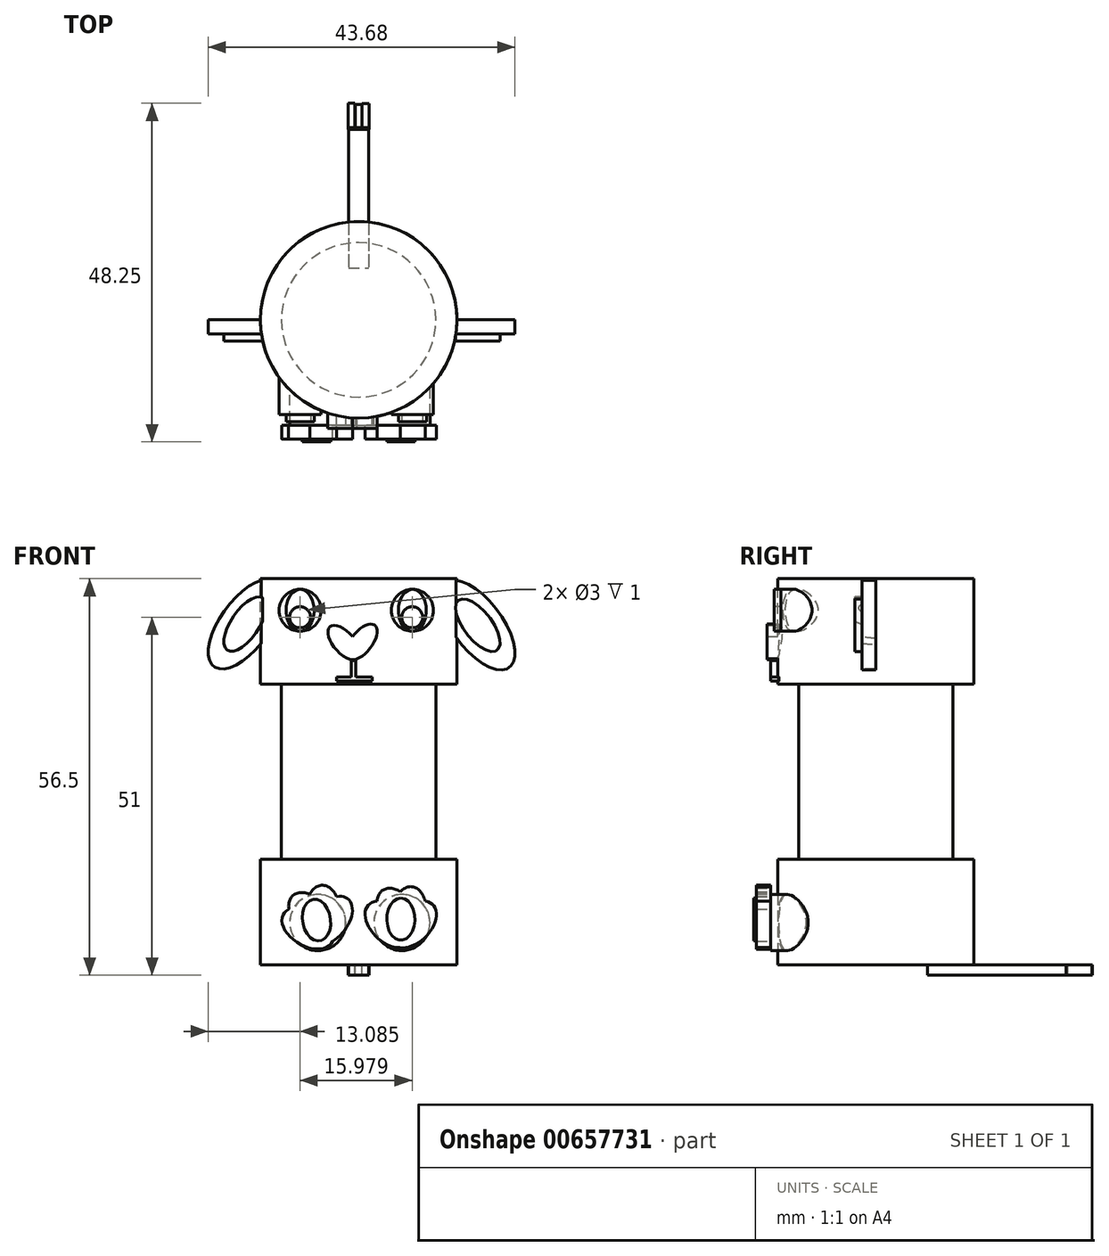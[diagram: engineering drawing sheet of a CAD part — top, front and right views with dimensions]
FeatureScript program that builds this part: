
annotation { "Feature Type Name" : "Feature", "Feature Type Description" : "" }
export const myFeature = defineFeature(function(context is Context, id is Id, definition is map)
    precondition{}
    {
        {
            var Q0;
            Q0=qCreatedBy(makeId("Top.planeOp"),FACE);
            var sketch = newSketch(context, id + "F0", { "sketchPlane" : qUnion([Q0])});
            skCircle(sketch, "E0", {"center": v(0, 0) * mm, "radius": 14 * mm});
            skSolve(sketch);
        }
        {
            var Q0;
            Q0 = qSketchRegion(id + "F0", true);
            extrude(context, id + "F1", {"entities" : qUnion([Q0]), "depth" : 15 * mm, "offsetDistance" : 25 * mm});
        }
        {
            var Q0;
            Q0=qCreatedBy(makeId("Top.planeOp"),FACE);
            var sketch = newSketch(context, id + "F2", { "sketchPlane" : qUnion([Q0])});
            skCircle(sketch, "E1", {"center": v(0, 0) * mm, "radius": 11 * mm});
            skSolve(sketch);
        }
        {
            var Q0;
            Q0 = qSketchRegion(id + "F2", true);
            extrude(context, id + "F3", {"entities" : qUnion([Q0]), "operationType" : NewBodyOperationType.REMOVE, "depth" : 45 * mm, "offsetDistance" : 25 * mm, "hasSecondDirection" : true, "secondDirectionOppositeDirection" : false, "secondDirectionDepth" : 5 * mm});
        }
        {
            var Q0;
            Q0=makeQuery(id+"F3.boolean.opBoolean","COPY",FACE,{"derivedFrom":makeQuery(id+"F3.opExtrude","CAP_FACE",FACE,{"disambiguationData":[OSD([sQuery(id+"F2.wireOp",EDGE,"E1")])],"isStart":true})});
            var sketch = newSketch(context, id + "F4", { "sketchPlane" : qUnion([Q0])});
            skCircle(sketch, "E2", {"center": v(0, 0) * mm, "radius": 11 * mm});
            skSolve(sketch);
        }
        {
            var Q0;
            Q0 = qSketchRegion(id + "F4", true);
            extrude(context, id + "F5", {"entities" : qUnion([Q0]), "operationType" : NewBodyOperationType.ADD, "depth" : 45 * mm, "offsetDistance" : 25 * mm});
        }
        {
            var Q0;
            Q0=makeQuery(id+"F5.opExtrude","CAP_FACE",FACE,{"disambiguationData":[OSD([sQuery(id+"F4.wireOp",EDGE,"E2")])],"isStart":false});
            var sketch = newSketch(context, id + "F6", { "sketchPlane" : qUnion([Q0])});
            skCircle(sketch, "E3", {"center": v(0, 0) * mm, "radius": 14 * mm});
            skSolve(sketch);
        }
        {
            var Q0;
            Q0 = qSketchRegion(id + "F6", true);
            extrude(context, id + "F7", {"entities" : qUnion([Q0]), "operationType" : NewBodyOperationType.ADD, "oppositeDirection" : true, "depth" : 10 * mm, "offsetDistance" : 25 * mm, "hasSecondDirection" : true, "secondDirectionOppositeDirection" : false, "secondDirectionDepth" : 5 * mm});
        }
        {
            var Q0;
            Q0=qCreatedBy(makeId("Front.planeOp"),FACE);
            var sketch = newSketch(context, id + "F8", { "sketchPlane" : qUnion([Q0])});
            skEllipse(sketch, "E4", {"center": v(16.98, 48.38) * mm, "majorRadius": 7.5 * mm, "minorRadius": 3.5 * mm, "majorAxis": v(0.6, -0.8)});
            skSolve(sketch);
        }
        {
            var Q0;
            Q0=makeQuery(id+"F8.imprint","IMPRINT",FACE,{"disambiguationData":[TD([[makeQuery(id+"F8.imprint","IMPRINT",EDGE,{"derivedFrom":sQuery(id+"F8.wireOp",EDGE,"E4")}),1.0]])]});
            extrude(context, id + "F9", {"entities" : qUnion([Q0]), "operationType" : NewBodyOperationType.ADD, "depth" : 2 * mm, "offsetDistance" : 25 * mm});
        }
        {
            var Q0;
            Q0=qCreatedBy(makeId("Front.planeOp"),FACE);
            var sketch = newSketch(context, id + "F10", { "sketchPlane" : qUnion([Q0])});
            skEllipse(sketch, "E5", {"center": v(-16.18, 48.54) * mm, "majorRadius": 7.5 * mm, "minorRadius": 3.5 * mm, "majorAxis": v(-0.59, -0.8)});
            skSolve(sketch);
        }
        {
            var Q0;
            Q0 = qSketchRegion(id + "F10", true);
            extrude(context, id + "F11", {"entities" : qUnion([Q0]), "operationType" : NewBodyOperationType.ADD, "depth" : 2 * mm, "offsetDistance" : 25 * mm});
        }
        {
            var Q0;
            Q0=qCreatedBy(makeId("Front.planeOp"),FACE);
            var sketch = newSketch(context, id + "F12", { "sketchPlane" : qUnion([Q0])});
            skEllipse(sketch, "E6", {"center": v(-2.1, 45.9) * mm, "majorRadius": 1.5 * mm, "minorRadius": 3 * mm, "majorAxis": v(-0.75, -0.66)});
            skEllipse(sketch, "E7", {"center": v(0.45, 46) * mm, "majorRadius": 1.5 * mm, "minorRadius": 3 * mm, "majorAxis": v(0.8, -0.61)});
            skSolve(sketch);
        }
        {
            var Q0;
            Q0 = qSketchRegion(id + "F12", true);
            extrude(context, id + "F13", {"entities" : qUnion([Q0]), "operationType" : NewBodyOperationType.ADD, "depth" : 15.5 * mm, "offsetDistance" : 25 * mm});
        }
        {
            var Q0;
            Q0=qCreatedBy(makeId("Front.planeOp"),FACE);
            var sketch = newSketch(context, id + "F14", { "sketchPlane" : qUnion([Q0])});
            skCircle(sketch, "E8", {"center": v(-8.34, 50.5) * mm, "radius": 3 * mm});
            skCircle(sketch, "E9", {"center": v(7.66, 50.5) * mm, "radius": 3 * mm});
            skSolve(sketch);
        }
        {
            var Q0;
            Q0 = qSketchRegion(id + "F14", true);
            extrude(context, id + "F15", {"entities" : qUnion([Q0]), "operationType" : NewBodyOperationType.ADD, "depth" : 13.5 * mm, "offsetDistance" : 25 * mm});
        }
        {
            var Q0;
            Q0=qCreatedBy(makeId("Front.planeOp"),FACE);
            var sketch = newSketch(context, id + "F16", { "sketchPlane" : qUnion([Q0])});
            skCircle(sketch, "E10", {"center": v(-5.83, 6) * mm, "radius": 4 * mm});
            skCircle(sketch, "E11", {"center": v(6.17, 6) * mm, "radius": 4 * mm});
            skSolve(sketch);
        }
        {
            var Q0;
            Q0 = qSketchRegion(id + "F16", true);
            extrude(context, id + "F17", {"entities" : qUnion([Q0]), "operationType" : NewBodyOperationType.ADD, "depth" : 15 * mm, "offsetDistance" : 25 * mm});
        }
        {
            var Q0;
            Q0=makeQuery(id+"F17.opExtrude","CAP_FACE",FACE,{"disambiguationData":[OSD([sQuery(id+"F16.wireOp",EDGE,"E11")])],"isStart":false});
            var sketch = newSketch(context, id + "F18", { "sketchPlane" : qUnion([Q0])});
            skEllipse(sketch, "E12", {"center": v(7.02, 7.16) * mm, "majorRadius": 4 * mm, "minorRadius": 2.5 * mm, "majorAxis": v(0.19, 0.98)});
            skEllipse(sketch, "E13", {"center": v(5.57, 7.22) * mm, "majorRadius": 4 * mm, "minorRadius": 2.5 * mm, "majorAxis": v(0.51, -0.86)});
            skEllipse(sketch, "E14", {"center": v(4.27, 5.74) * mm, "majorRadius": 4 * mm, "minorRadius": 2.5 * mm, "majorAxis": v(-0.72, 0.7)});
            skEllipse(sketch, "E15", {"center": v(7.74, 5.72) * mm, "majorRadius": 4 * mm, "minorRadius": 2.5 * mm, "majorAxis": v(0.71, 0.7)});
            skSolve(sketch);
        }
        {
            var Q0;
            {var subQ0=sQuery(id+"F18.wireOp",EDGE,"E13");var subQ1=sQuery(id+"F18.wireOp",EDGE,"E12");var subQ2=makeQuery(id+"F18.imprint","INTERSECT",VERTEX,{"disambiguationData":[OD(1.0)],"derivedFrom":[subQ1,subQ0]});Q0=makeQuery(id+"F18.imprint","IMPRINT",FACE,{"disambiguationData":[TD([[makeQuery(id+"F18.imprint","IMPRINT",EDGE,{"disambiguationData":[TD([[subQ2,-1.0]])],"derivedFrom":subQ1}),-1.0]])]});}
            var Q1;
            {var subQ0=sQuery(id+"F18.wireOp",EDGE,"E15");var subQ1=sQuery(id+"F18.wireOp",EDGE,"E12");var subQ2=makeQuery(id+"F18.imprint","INTERSECT",VERTEX,{"disambiguationData":[OD(0.0)],"derivedFrom":[subQ1,subQ0]});Q1=makeQuery(id+"F18.imprint","IMPRINT",FACE,{"disambiguationData":[TD([[makeQuery(id+"F18.imprint","IMPRINT",EDGE,{"disambiguationData":[TD([[subQ2,1.0]])],"derivedFrom":subQ1}),-1.0]])]});}
            var Q2;
            {var subQ0=sQuery(id+"F18.wireOp",EDGE,"E14");var subQ1=sQuery(id+"F18.wireOp",EDGE,"E13");var subQ2=makeQuery(id+"F18.imprint","INTERSECT",VERTEX,{"disambiguationData":[OD(0.0)],"derivedFrom":[subQ1,subQ0]});Q2=makeQuery(id+"F18.imprint","IMPRINT",FACE,{"disambiguationData":[TD([[makeQuery(id+"F18.imprint","IMPRINT",EDGE,{"disambiguationData":[TD([[subQ2,-1.0]])],"derivedFrom":subQ1}),-1.0]])]});}
            var Q3;
            {var subQ0=sQuery(id+"F18.wireOp",EDGE,"E13");var subQ1=sQuery(id+"F18.wireOp",EDGE,"E12");var subQ2=makeQuery(id+"F18.imprint","INTERSECT",VERTEX,{"disambiguationData":[OD(0.0)],"derivedFrom":[subQ1,subQ0]});Q3=makeQuery(id+"F18.imprint","IMPRINT",FACE,{"disambiguationData":[TD([[makeQuery(id+"F18.imprint","IMPRINT",EDGE,{"disambiguationData":[TD([[subQ2,-1.0]])],"derivedFrom":subQ1}),1.0]])]});}
            var Q4;
            {var subQ0=sQuery(id+"F18.wireOp",EDGE,"E13");var subQ1=sQuery(id+"F18.wireOp",EDGE,"E12");var subQ2=makeQuery(id+"F18.imprint","INTERSECT",VERTEX,{"disambiguationData":[OD(0.0)],"derivedFrom":[subQ1,subQ0]});Q4=makeQuery(id+"F18.imprint","IMPRINT",FACE,{"disambiguationData":[TD([[makeQuery(id+"F18.imprint","IMPRINT",EDGE,{"disambiguationData":[TD([[subQ2,-1.0]])],"derivedFrom":subQ1}),-1.0]])]});}
            var Q5;
            {var subQ0=sQuery(id+"F18.wireOp",EDGE,"E14");var subQ1=sQuery(id+"F18.wireOp",EDGE,"E12");var subQ2=makeQuery(id+"F18.imprint","INTERSECT",VERTEX,{"disambiguationData":[OD(0.0)],"derivedFrom":[subQ1,subQ0]});Q5=makeQuery(id+"F18.imprint","IMPRINT",FACE,{"disambiguationData":[TD([[makeQuery(id+"F18.imprint","IMPRINT",EDGE,{"disambiguationData":[TD([[subQ2,1.0]])],"derivedFrom":subQ1}),-1.0]])]});}
            var Q6;
            {var subQ0=sQuery(id+"F18.wireOp",EDGE,"E15");var subQ1=sQuery(id+"F18.wireOp",EDGE,"E12");var subQ2=makeQuery(id+"F18.imprint","INTERSECT",VERTEX,{"disambiguationData":[OD(0.0)],"derivedFrom":[subQ1,subQ0]});Q6=makeQuery(id+"F18.imprint","IMPRINT",FACE,{"disambiguationData":[TD([[makeQuery(id+"F18.imprint","IMPRINT",EDGE,{"disambiguationData":[TD([[subQ2,1.0]])],"derivedFrom":subQ1}),1.0]])]});}
            var Q7;
            {var subQ0=sQuery(id+"F18.wireOp",EDGE,"E13");var subQ1=sQuery(id+"F18.wireOp",EDGE,"E12");var subQ2=makeQuery(id+"F18.imprint","INTERSECT",VERTEX,{"disambiguationData":[OD(0.0)],"derivedFrom":[subQ1,subQ0]});Q7=makeQuery(id+"F18.imprint","IMPRINT",FACE,{"disambiguationData":[TD([[makeQuery(id+"F18.imprint","IMPRINT",EDGE,{"disambiguationData":[TD([[subQ2,1.0]])],"derivedFrom":subQ1}),1.0]])]});}
            var Q8;
            {var subQ0=sQuery(id+"F18.wireOp",EDGE,"E15");var subQ1=sQuery(id+"F18.wireOp",EDGE,"E13");var subQ2=makeQuery(id+"F18.imprint","INTERSECT",VERTEX,{"disambiguationData":[OD(0.0)],"derivedFrom":[subQ1,subQ0]});Q8=makeQuery(id+"F18.imprint","IMPRINT",FACE,{"disambiguationData":[TD([[makeQuery(id+"F18.imprint","IMPRINT",EDGE,{"disambiguationData":[TD([[subQ2,-1.0]])],"derivedFrom":subQ1}),-1.0]])]});}
            var Q9;
            {var subQ0=sQuery(id+"F18.wireOp",EDGE,"E14");var subQ1=sQuery(id+"F18.wireOp",EDGE,"E13");var subQ2=makeQuery(id+"F18.imprint","INTERSECT",VERTEX,{"disambiguationData":[OD(0.0)],"derivedFrom":[subQ1,subQ0]});Q9=makeQuery(id+"F18.imprint","IMPRINT",FACE,{"disambiguationData":[TD([[makeQuery(id+"F18.imprint","IMPRINT",EDGE,{"disambiguationData":[TD([[subQ2,-1.0]])],"derivedFrom":subQ1}),1.0]])]});}
            var Q10;
            {var subQ0=sQuery(id+"F18.wireOp",EDGE,"E14");var subQ1=sQuery(id+"F18.wireOp",EDGE,"E12");var subQ2=makeQuery(id+"F18.imprint","INTERSECT",VERTEX,{"disambiguationData":[OD(1.0)],"derivedFrom":[subQ1,subQ0]});Q10=makeQuery(id+"F18.imprint","IMPRINT",FACE,{"disambiguationData":[TD([[makeQuery(id+"F18.imprint","IMPRINT",EDGE,{"disambiguationData":[TD([[subQ2,-1.0]])],"derivedFrom":subQ1}),-1.0]])]});}
            var Q11;
            {var subQ0=sQuery(id+"F18.wireOp",EDGE,"E15");var subQ1=sQuery(id+"F18.wireOp",EDGE,"E13");var subQ2=makeQuery(id+"F18.imprint","INTERSECT",VERTEX,{"disambiguationData":[OD(1.0)],"derivedFrom":[subQ1,subQ0]});Q11=makeQuery(id+"F18.imprint","IMPRINT",FACE,{"disambiguationData":[TD([[makeQuery(id+"F18.imprint","IMPRINT",EDGE,{"disambiguationData":[TD([[subQ2,1.0]])],"derivedFrom":subQ1}),-1.0]])]});}
            var Q12;
            {var subQ0=sQuery(id+"F18.wireOp",EDGE,"E14");var subQ1=sQuery(id+"F18.wireOp",EDGE,"E12");var subQ2=makeQuery(id+"F18.imprint","INTERSECT",VERTEX,{"disambiguationData":[OD(0.0)],"derivedFrom":[subQ1,subQ0]});Q12=makeQuery(id+"F18.imprint","IMPRINT",FACE,{"disambiguationData":[TD([[makeQuery(id+"F18.imprint","IMPRINT",EDGE,{"disambiguationData":[TD([[subQ2,1.0]])],"derivedFrom":subQ1}),1.0]])]});}
            var Q13;
            {var subQ0=sQuery(id+"F18.wireOp",EDGE,"E14");var subQ1=sQuery(id+"F18.wireOp",EDGE,"E12");var subQ2=makeQuery(id+"F18.imprint","INTERSECT",VERTEX,{"disambiguationData":[OD(1.0)],"derivedFrom":[subQ1,subQ0]});Q13=makeQuery(id+"F18.imprint","IMPRINT",FACE,{"disambiguationData":[TD([[makeQuery(id+"F18.imprint","IMPRINT",EDGE,{"disambiguationData":[TD([[subQ2,-1.0]])],"derivedFrom":subQ1}),1.0]])]});}
            var Q14;
            {var subQ0=sQuery(id+"F18.wireOp",EDGE,"E15");var subQ1=sQuery(id+"F18.wireOp",EDGE,"E12");var subQ2=makeQuery(id+"F18.imprint","INTERSECT",VERTEX,{"disambiguationData":[OD(1.0)],"derivedFrom":[subQ1,subQ0]});Q14=makeQuery(id+"F18.imprint","IMPRINT",FACE,{"disambiguationData":[TD([[makeQuery(id+"F18.imprint","IMPRINT",EDGE,{"disambiguationData":[TD([[subQ2,-1.0]])],"derivedFrom":subQ1}),1.0]])]});}
            var Q15;
            {var subQ0=sQuery(id+"F18.wireOp",EDGE,"E14");var subQ1=sQuery(id+"F18.wireOp",EDGE,"E12");var subQ2=makeQuery(id+"F18.imprint","INTERSECT",VERTEX,{"disambiguationData":[OD(0.0)],"derivedFrom":[subQ1,subQ0]});Q15=makeQuery(id+"F18.imprint","IMPRINT",FACE,{"disambiguationData":[TD([[makeQuery(id+"F18.imprint","IMPRINT",EDGE,{"disambiguationData":[TD([[subQ2,-1.0]])],"derivedFrom":subQ1}),1.0]])]});}
            var Q16;
            {var subQ0=sQuery(id+"F18.wireOp",EDGE,"E15");var subQ1=sQuery(id+"F18.wireOp",EDGE,"E13");var subQ2=makeQuery(id+"F18.imprint","INTERSECT",VERTEX,{"disambiguationData":[OD(0.0)],"derivedFrom":[subQ1,subQ0]});Q16=makeQuery(id+"F18.imprint","IMPRINT",FACE,{"disambiguationData":[TD([[makeQuery(id+"F18.imprint","IMPRINT",EDGE,{"disambiguationData":[TD([[subQ2,1.0]])],"derivedFrom":subQ1}),1.0]])]});}
            var Q17;
            {var subQ1=sQuery(id+"F18.wireOp",EDGE,"E12");var subQ7=sQuery(id+"F18.wireOp",EDGE,"E14");var subQ9=makeQuery(id+"F18.imprint","INTERSECT",VERTEX,{"disambiguationData":[OD(0.0)],"derivedFrom":[subQ1,subQ7]});Q17=makeQuery(id+"F18.imprint","IMPRINT",FACE,{"disambiguationData":[TD([[makeQuery(id+"F18.imprint","IMPRINT",EDGE,{"disambiguationData":[TD([[subQ9,-1.0]])],"derivedFrom":subQ1}),-1.0]])]});}
            var Q18;
            {var subQ0=sQuery(id+"F18.wireOp",EDGE,"E13");var subQ1=sQuery(id+"F18.wireOp",EDGE,"E12");var subQ2=makeQuery(id+"F18.imprint","INTERSECT",VERTEX,{"disambiguationData":[OD(1.0)],"derivedFrom":[subQ1,subQ0]});Q18=makeQuery(id+"F18.imprint","IMPRINT",FACE,{"disambiguationData":[TD([[makeQuery(id+"F18.imprint","IMPRINT",EDGE,{"disambiguationData":[TD([[subQ2,-1.0]])],"derivedFrom":subQ1}),1.0]])]});}
            var Q19;
            {var subQ0=sQuery(id+"F18.wireOp",EDGE,"E15");var subQ1=sQuery(id+"F18.wireOp",EDGE,"E12");var subQ2=makeQuery(id+"F18.imprint","INTERSECT",VERTEX,{"disambiguationData":[OD(1.0)],"derivedFrom":[subQ1,subQ0]});Q19=makeQuery(id+"F18.imprint","IMPRINT",FACE,{"disambiguationData":[TD([[makeQuery(id+"F18.imprint","IMPRINT",EDGE,{"disambiguationData":[TD([[subQ2,-1.0]])],"derivedFrom":subQ1}),-1.0]])]});}
            extrude(context, id + "F19", {"entities" : qUnion([Q0, Q1, Q2, Q3, Q4, Q5, Q6, Q7, Q8, Q9, Q10, Q11, Q12, Q13, Q14, Q15, Q16, Q17, Q18, Q19]), "operationType" : NewBodyOperationType.ADD, "depth" : 2 * mm, "offsetDistance" : 25 * mm});
        }
        {
            var Q0;
            Q0=makeQuery(id+"F17.opExtrude","CAP_FACE",FACE,{"disambiguationData":[OSD([sQuery(id+"F16.wireOp",EDGE,"E10")])],"isStart":false});
            var sketch = newSketch(context, id + "F20", { "sketchPlane" : qUnion([Q0])});
            skEllipse(sketch, "E16", {"center": v(-4.1, 6.29) * mm, "majorRadius": 4 * mm, "minorRadius": 2.5 * mm, "majorAxis": v(0.64, 0.77)});
            skEllipse(sketch, "E17", {"center": v(-5.16, 7.32) * mm, "majorRadius": 4 * mm, "minorRadius": 2.5 * mm, "majorAxis": v(0, 1)});
            skEllipse(sketch, "E18", {"center": v(-6.7, 6.87) * mm, "majorRadius": 4 * mm, "minorRadius": 2.5 * mm, "majorAxis": v(0.67, -0.74)});
            skEllipse(sketch, "E19", {"center": v(-7.27, 5.19) * mm, "majorRadius": 4 * mm, "minorRadius": 2.5 * mm, "majorAxis": v(-0.86, 0.5)});
            skPoint(sketch, "E20", {"position": v(-8.55, 5.19) * mm});
            skSolve(sketch);
        }
        {
            var Q0;
            Q0 = qSketchRegion(id + "F20", true);
            var Q1;
            {var subQ0=sQuery(id+"F20.wireOp",EDGE,"E18");var subQ1=sQuery(id+"F20.wireOp",EDGE,"E16");var subQ2=makeQuery(id+"F20.imprint","INTERSECT",VERTEX,{"disambiguationData":[OD(0.0)],"derivedFrom":[subQ1,subQ0]});Q1=makeQuery(id+"F20.imprint","IMPRINT",FACE,{"disambiguationData":[TD([[makeQuery(id+"F20.imprint","IMPRINT",EDGE,{"disambiguationData":[TD([[subQ2,-1.0]])],"derivedFrom":subQ1}),1.0]])]});}
            var Q2;
            {var subQ0=sQuery(id+"F20.wireOp",EDGE,"E19");var subQ1=sQuery(id+"F20.wireOp",EDGE,"E16");var subQ2=makeQuery(id+"F20.imprint","INTERSECT",VERTEX,{"disambiguationData":[OD(0.0)],"derivedFrom":[subQ1,subQ0]});Q2=makeQuery(id+"F20.imprint","IMPRINT",FACE,{"disambiguationData":[TD([[makeQuery(id+"F20.imprint","IMPRINT",EDGE,{"disambiguationData":[TD([[subQ2,-1.0]])],"derivedFrom":subQ1}),1.0]])]});}
            var Q3;
            {var subQ0=sQuery(id+"F20.wireOp",EDGE,"E19");var subQ1=sQuery(id+"F20.wireOp",EDGE,"E16");var subQ2=makeQuery(id+"F20.imprint","INTERSECT",VERTEX,{"disambiguationData":[OD(0.0)],"derivedFrom":[subQ1,subQ0]});Q3=makeQuery(id+"F20.imprint","IMPRINT",FACE,{"disambiguationData":[TD([[makeQuery(id+"F20.imprint","IMPRINT",EDGE,{"disambiguationData":[TD([[subQ2,-1.0]])],"derivedFrom":subQ1}),-1.0]])]});}
            var Q4;
            {var subQ0=sQuery(id+"F20.wireOp",EDGE,"E17");var subQ1=sQuery(id+"F20.wireOp",EDGE,"E16");var subQ2=makeQuery(id+"F20.imprint","INTERSECT",VERTEX,{"disambiguationData":[OD(1.0)],"derivedFrom":[subQ1,subQ0]});Q4=makeQuery(id+"F20.imprint","IMPRINT",FACE,{"disambiguationData":[TD([[makeQuery(id+"F20.imprint","IMPRINT",EDGE,{"disambiguationData":[TD([[subQ2,-1.0]])],"derivedFrom":subQ1}),1.0]])]});}
            var Q5;
            {var subQ0=sQuery(id+"F20.wireOp",EDGE,"E18");var subQ1=sQuery(id+"F20.wireOp",EDGE,"E17");var subQ2=makeQuery(id+"F20.imprint","INTERSECT",VERTEX,{"disambiguationData":[OD(1.0)],"derivedFrom":[subQ1,subQ0]});Q5=makeQuery(id+"F20.imprint","IMPRINT",FACE,{"disambiguationData":[TD([[makeQuery(id+"F20.imprint","IMPRINT",EDGE,{"disambiguationData":[TD([[subQ2,-1.0]])],"derivedFrom":subQ1}),1.0]])]});}
            extrude(context, id + "F21", {"entities" : qUnion([Q0, Q1, Q2, Q3, Q4, Q5]), "operationType" : NewBodyOperationType.ADD, "depth" : 2 * mm, "offsetDistance" : 25 * mm});
        }
        {
            var Q0;
            Q0=makeQuery(id+"F15.opExtrude","CAP_FACE",FACE,{"disambiguationData":[OSD([sQuery(id+"F14.wireOp",EDGE,"E8")])],"isStart":false});
            var sketch = newSketch(context, id + "F22", { "sketchPlane" : qUnion([Q0])});
            skEllipse(sketch, "E21", {"center": v(-8.34, 50.5) * mm, "majorRadius": 3 * mm, "minorRadius": 2 * mm, "majorAxis": v(0, 1)});
            skSolve(sketch);
        }
        {
            var Q0;
            Q0 = qSketchRegion(id + "F22", true);
            extrude(context, id + "F23", {"entities" : qUnion([Q0]), "operationType" : NewBodyOperationType.ADD, "depth" : 1 * mm, "offsetDistance" : 25 * mm});
        }
        {
            var Q0;
            Q0=makeQuery(id+"F15.opExtrude","CAP_FACE",FACE,{"disambiguationData":[OSD([sQuery(id+"F14.wireOp",EDGE,"E9")])],"isStart":false});
            var sketch = newSketch(context, id + "F24", { "sketchPlane" : qUnion([Q0])});
            skEllipse(sketch, "E22", {"center": v(7.66, 50.5) * mm, "majorRadius": 3 * mm, "minorRadius": 2 * mm, "majorAxis": v(0, 1)});
            skSolve(sketch);
        }
        {
            var Q0;
            Q0 = qSketchRegion(id + "F24", true);
            extrude(context, id + "F25", {"entities" : qUnion([Q0]), "operationType" : NewBodyOperationType.ADD, "depth" : 1 * mm, "offsetDistance" : 25 * mm});
        }
        {
            var Q0;
            Q0=makeQuery(id+"F23.opExtrude","CAP_FACE",FACE,{"disambiguationData":[OSD([sQuery(id+"F22.wireOp",EDGE,"E21")])],"isStart":false});
            var sketch = newSketch(context, id + "F26", { "sketchPlane" : qUnion([Q0])});
            skCircle(sketch, "E23", {"center": v(-8.34, 49.5) * mm, "radius": 1.5 * mm});
            skSolve(sketch);
        }
        {
            var Q0;
            Q0 = qSketchRegion(id + "F26", true);
            extrude(context, id + "F27", {"entities" : qUnion([Q0]), "operationType" : NewBodyOperationType.REMOVE, "oppositeDirection" : true, "depth" : 1 * mm, "offsetDistance" : 25 * mm});
        }
        {
            var Q0;
            Q0=makeQuery(id+"F25.opExtrude","CAP_FACE",FACE,{"disambiguationData":[OSD([sQuery(id+"F24.wireOp",EDGE,"E22")])],"isStart":false});
            var sketch = newSketch(context, id + "F28", { "sketchPlane" : qUnion([Q0])});
            skCircle(sketch, "E24", {"center": v(7.63, 49.5) * mm, "radius": 1.5 * mm});
            skSolve(sketch);
        }
        {
            var Q0;
            Q0 = qSketchRegion(id + "F28", true);
            extrude(context, id + "F29", {"entities" : qUnion([Q0]), "operationType" : NewBodyOperationType.REMOVE, "oppositeDirection" : true, "depth" : 1 * mm, "offsetDistance" : 25 * mm});
        }
        {
            var Q0;
            Q0=makeQuery(id+"F11.opExtrude","CAP_FACE",FACE,{"disambiguationData":[OSD([sQuery(id+"F10.wireOp",EDGE,"E5")])],"isStart":false});
            var sketch = newSketch(context, id + "F30", { "sketchPlane" : qUnion([Q0])});
            skEllipse(sketch, "E25", {"center": v(-16.18, 48.54) * mm, "majorRadius": 4.5 * mm, "minorRadius": 2 * mm, "majorAxis": v(0.56, 0.83)});
            skSolve(sketch);
        }
        {
            var Q0;
            Q0 = qSketchRegion(id + "F30", true);
            extrude(context, id + "F31", {"entities" : qUnion([Q0]), "operationType" : NewBodyOperationType.ADD, "depth" : 1 * mm, "offsetDistance" : 25 * mm});
        }
        {
            var Q0;
            Q0=makeQuery(id+"F9.opExtrude","CAP_FACE",FACE,{"disambiguationData":[OSD([sQuery(id+"F8.wireOp",EDGE,"E4")])],"isStart":false});
            var sketch = newSketch(context, id + "F32", { "sketchPlane" : qUnion([Q0])});
            skEllipse(sketch, "E26", {"center": v(16.98, 48.38) * mm, "majorRadius": 4.5 * mm, "minorRadius": 2 * mm, "majorAxis": v(-0.62, 0.79)});
            skSolve(sketch);
        }
        {
            var Q0;
            Q0 = qSketchRegion(id + "F32", true);
            extrude(context, id + "F33", {"entities" : qUnion([Q0]), "operationType" : NewBodyOperationType.ADD, "depth" : 1 * mm, "offsetDistance" : 25 * mm});
        }
        {
            var Q0;
            Q0=qCreatedBy(makeId("Top.planeOp"),FACE);
            var sketch = newSketch(context, id + "F34", { "sketchPlane" : qUnion([Q0])});
            skLineSegment(sketch, "E27.bottom", {"start": v(-1.4, 27.39) * mm, "end": v(1.4, 27.39) * mm});
            skLineSegment(sketch, "E27.top", {"start": v(-1.4, 7.39) * mm, "end": v(1.4, 7.39) * mm});
            skLineSegment(sketch, "E27.left", {"start": v(-1.4, 27.39) * mm, "end": v(-1.4, 7.39) * mm});
            skLineSegment(sketch, "E27.right", {"start": v(1.4, 27.39) * mm, "end": v(1.4, 7.39) * mm});
            skPoint(sketch, "E27.middle", {"position": v(0, 17.39) * mm});
            skSolve(sketch);
        }
        {
            var Q0;
            Q0 = qSketchRegion(id + "F34", true);
            extrude(context, id + "F35", {"entities" : qUnion([Q0]), "operationType" : NewBodyOperationType.ADD, "oppositeDirection" : true, "depth" : 1.5 * mm, "offsetDistance" : 25 * mm});
        }
        {
            var Q0;
            Q0=qCreatedBy(makeId("Top.planeOp"),FACE);
            var sketch = newSketch(context, id + "F36", { "sketchPlane" : qUnion([Q0])});
            skLineSegment(sketch, "E28.bottom", {"start": v(0.5, 30.82) * mm, "end": v(1.5, 30.82) * mm});
            skLineSegment(sketch, "E28.top", {"start": v(0.5, 27.14) * mm, "end": v(1.5, 27.14) * mm});
            skLineSegment(sketch, "E28.left", {"start": v(0.5, 30.82) * mm, "end": v(0.5, 27.14) * mm});
            skLineSegment(sketch, "E28.right", {"start": v(1.5, 30.82) * mm, "end": v(1.5, 27.14) * mm});
            skPoint(sketch, "E28.middle", {"position": v(1, 28.98) * mm});
            skLineSegment(sketch, "E29.bottom", {"start": v(-0.5, 27.14) * mm, "end": v(0.5, 27.14) * mm});
            skLineSegment(sketch, "E29.top", {"start": v(-0.5, 30.71) * mm, "end": v(0.5, 30.71) * mm});
            skLineSegment(sketch, "E29.left", {"start": v(-0.5, 27.14) * mm, "end": v(-0.5, 30.71) * mm});
            skLineSegment(sketch, "E29.right", {"start": v(0.5, 27.14) * mm, "end": v(0.5, 30.71) * mm});
            skPoint(sketch, "E29.middle", {"position": v(0, 28.93) * mm});
            skLineSegment(sketch, "E30.bottom", {"start": v(-1.49, 27.14) * mm, "end": v(-0.53, 27.14) * mm});
            skLineSegment(sketch, "E30.top", {"start": v(-1.49, 30.85) * mm, "end": v(-0.53, 30.85) * mm});
            skLineSegment(sketch, "E30.left", {"start": v(-1.49, 27.14) * mm, "end": v(-1.49, 30.85) * mm});
            skLineSegment(sketch, "E30.right", {"start": v(-0.53, 27.14) * mm, "end": v(-0.53, 30.85) * mm});
            skPoint(sketch, "E30.middle", {"position": v(-1, 29) * mm});
            skSolve(sketch);
        }
        {
            var Q0;
            Q0 = qSketchRegion(id + "F36", true);
            extrude(context, id + "F37", {"entities" : qUnion([Q0]), "oppositeDirection" : true, "depth" : 1.5 * mm, "offsetDistance" : 25 * mm});
        }
        {
            var Q0;
            Q0=makeQuery(id+"F21.opExtrude","CAP_FACE",FACE,{"disambiguationData":[OSD([sQuery(id+"F20.wireOp",EDGE,"E16"),sQuery(id+"F20.wireOp",EDGE,"E17"),sQuery(id+"F20.wireOp",EDGE,"E18"),sQuery(id+"F20.wireOp",EDGE,"E19")])],"isStart":false});
            var sketch = newSketch(context, id + "F38", { "sketchPlane" : qUnion([Q0])});
            skEllipse(sketch, "E31", {"center": v(-6, 6.35) * mm, "majorRadius": 3 * mm, "minorRadius": 1.99 * mm, "majorAxis": v(-0.16, 0.99)});
            skPoint(sketch, "E31.centerSnap0", {"position": v(-6, 7.34) * mm});
            skSolve(sketch);
        }
        {
            var Q0;
            Q0=makeQuery(id+"F38.imprint","IMPRINT",FACE,{"disambiguationData":[TD([[makeQuery(id+"F38.imprint","IMPRINT",EDGE,{"derivedFrom":sQuery(id+"F38.wireOp",EDGE,"E31")}),1.0]])]});
            extrude(context, id + "F39", {"entities" : qUnion([Q0]), "operationType" : NewBodyOperationType.ADD, "depth" : .4 * mm, "offsetDistance" : 25 * mm});
        }
        {
            var Q0;
            Q0=makeQuery(id+"F19.opExtrude","CAP_FACE",FACE,{"disambiguationData":[OSD([sQuery(id+"F18.wireOp",EDGE,"E12"),sQuery(id+"F18.wireOp",EDGE,"E13"),sQuery(id+"F18.wireOp",EDGE,"E14"),sQuery(id+"F18.wireOp",EDGE,"E15")])],"isStart":false});
            var sketch = newSketch(context, id + "F40", { "sketchPlane" : qUnion([Q0])});
            skEllipse(sketch, "E32", {"center": v(6.01, 6.48) * mm, "majorRadius": 3 * mm, "minorRadius": 2 * mm, "majorAxis": v(0, 1)});
            skPoint(sketch, "E33", {"position": v(6.01, 7.54) * mm});
            skSolve(sketch);
        }
        {
            var Q0;
            Q0 = qSketchRegion(id + "F40", true);
            extrude(context, id + "F41", {"entities" : qUnion([Q0]), "operationType" : NewBodyOperationType.ADD, "depth" : .4 * mm, "offsetDistance" : 25 * mm});
        }
        {
            var Q0;
            Q0=qCreatedBy(makeId("Front.planeOp"),FACE);
            var sketch = newSketch(context, id + "F42", { "sketchPlane" : qUnion([Q0])});
            skLineSegment(sketch, "E34.bottom", {"start": v(-1.06, 43.33) * mm, "end": v(-0.42, 43.33) * mm});
            skLineSegment(sketch, "E34.top", {"start": v(-1.06, 40.65) * mm, "end": v(-0.42, 40.65) * mm});
            skLineSegment(sketch, "E34.left", {"start": v(-1.06, 43.33) * mm, "end": v(-1.06, 40.65) * mm});
            skLineSegment(sketch, "E34.right", {"start": v(-0.42, 43.33) * mm, "end": v(-0.42, 40.65) * mm});
            skSolve(sketch);
        }
        {
            var Q0;
            Q0 = qSketchRegion(id + "F42", true);
            extrude(context, id + "F43", {"entities" : qUnion([Q0]), "operationType" : NewBodyOperationType.ADD, "depth" : 15 * mm, "offsetDistance" : 25 * mm});
        }
        {
            var Q0;
            Q0=qCreatedBy(makeId("Front.planeOp"),FACE);
            var sketch = newSketch(context, id + "F44", { "sketchPlane" : qUnion([Q0])});
            skLineSegment(sketch, "E35.bottom", {"start": v(-3.11, 41.01) * mm, "end": v(1.95, 41.01) * mm});
            skLineSegment(sketch, "E35.top", {"start": v(-3.11, 40.44) * mm, "end": v(1.95, 40.44) * mm});
            skLineSegment(sketch, "E35.left", {"start": v(-3.11, 41.01) * mm, "end": v(-3.11, 40.44) * mm});
            skLineSegment(sketch, "E35.right", {"start": v(1.95, 41.01) * mm, "end": v(1.95, 40.44) * mm});
            skSolve(sketch);
        }
        {
            var Q0;
            Q0 = qSketchRegion(id + "F44", true);
            extrude(context, id + "F45", {"entities" : qUnion([Q0]), "operationType" : NewBodyOperationType.ADD, "depth" : 15 * mm, "offsetDistance" : 25 * mm});
        }
    });
